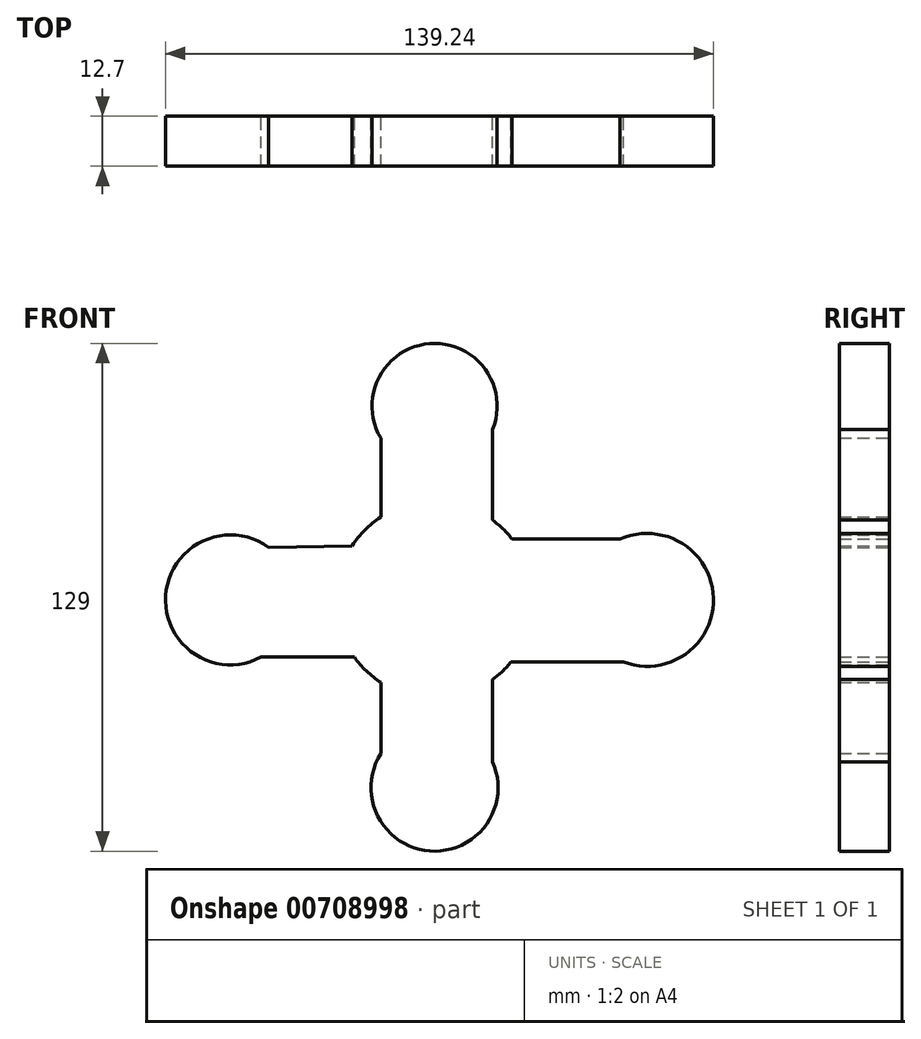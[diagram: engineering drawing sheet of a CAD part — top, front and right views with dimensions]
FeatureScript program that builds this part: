
annotation { "Feature Type Name" : "Feature", "Feature Type Description" : "" }
export const myFeature = defineFeature(function(context is Context, id is Id, definition is map)
    precondition{}
    {
        {
            var Q0;
            Q0=qCreatedBy(makeId("Front.planeOp"),FACE);
            var sketch = newSketch(context, id + "F0", { "sketchPlane" : qUnion([Q0])});
            skCircle(sketch, "E0", {"center": v(0, 0) * mm, "radius": 25.04 * mm});
            skCircle(sketch, "E1", {"center": v(0, 49.24) * mm, "radius": 15.9 * mm});
            skCircle(sketch, "E2", {"center": v(-51.87, 0) * mm, "radius": 16.5 * mm});
            skCircle(sketch, "E3", {"center": v(54, 0) * mm, "radius": 16.88 * mm});
            skCircle(sketch, "E4", {"center": v(0, -47.7) * mm, "radius": 16.15 * mm});
            skLineSegment(sketch, "E5", {"start": v(-13.64, 41.07) * mm, "end": v(-13.64, 21) * mm});
            skLineSegment(sketch, "E6", {"start": v(14.74, 43.26) * mm, "end": v(14.74, 20.24) * mm});
            skLineSegment(sketch, "E7", {"start": v(47.15, 15.42) * mm, "end": v(19.72, 15.42) * mm});
            skLineSegment(sketch, "E8", {"start": v(47.97, -15.76) * mm, "end": v(19.46, -15.76) * mm});
            skLineSegment(sketch, "E9", {"start": v(-13.64, -21) * mm, "end": v(-13.64, -39.07) * mm});
            skLineSegment(sketch, "E10", {"start": v(14.74, -20.24) * mm, "end": v(14.74, -44.36) * mm});
            skLineSegment(sketch, "E11", {"start": v(-42.2, 13.37) * mm, "end": v(-20.92, 13.75) * mm});
            skLineSegment(sketch, "E12", {"start": v(-44.1, -14.55) * mm, "end": v(-20.38, -14.55) * mm});
            skSolve(sketch);
        }
        {
            var Q0;
            {var subQ0=sQuery(id+"F0.wireOp",EDGE,"E4");var subQ1=makeQuery(id+"F0.imprint","INTERSECT",VERTEX,{"derivedFrom":[subQ0,sQuery(id+"F0.wireOp",EDGE,"E9")]});Q0=makeQuery(id+"F0.imprint","IMPRINT",FACE,{"disambiguationData":[TD([[makeQuery(id+"F0.imprint","IMPRINT",EDGE,{"disambiguationData":[TD([[subQ1,1.0]])],"derivedFrom":subQ0}),1.0]])]});}
            var Q1;
            {var subQ0=sQuery(id+"F0.wireOp",EDGE,"E1");var subQ1=makeQuery(id+"F0.imprint","INTERSECT",VERTEX,{"derivedFrom":[subQ0,sQuery(id+"F0.wireOp",EDGE,"E5")]});Q1=makeQuery(id+"F0.imprint","IMPRINT",FACE,{"disambiguationData":[TD([[makeQuery(id+"F0.imprint","IMPRINT",EDGE,{"disambiguationData":[TD([[subQ1,-1.0]])],"derivedFrom":subQ0}),1.0]])]});}
            var Q2;
            {var subQ0=sQuery(id+"F0.wireOp",EDGE,"E11");Q2=makeQuery(id+"F0.imprint","IMPRINT",FACE,{"disambiguationData":[TD([[makeQuery(id+"F0.imprint","IMPRINT",EDGE,{"derivedFrom":subQ0}),-1.0]])]});}
            var Q3;
            {var subQ0=sQuery(id+"F0.wireOp",EDGE,"E9");Q3=makeQuery(id+"F0.imprint","IMPRINT",FACE,{"disambiguationData":[TD([[makeQuery(id+"F0.imprint","IMPRINT",EDGE,{"derivedFrom":subQ0}),1.0]])]});}
            var Q4;
            {var subQ0=sQuery(id+"F0.wireOp",EDGE,"E3");var subQ1=makeQuery(id+"F0.imprint","INTERSECT",VERTEX,{"derivedFrom":[subQ0,sQuery(id+"F0.wireOp",EDGE,"E7")]});Q4=makeQuery(id+"F0.imprint","IMPRINT",FACE,{"disambiguationData":[TD([[makeQuery(id+"F0.imprint","IMPRINT",EDGE,{"disambiguationData":[TD([[subQ1,-1.0]])],"derivedFrom":subQ0}),1.0]])]});}
            var Q5;
            {var subQ0=sQuery(id+"F0.wireOp",EDGE,"E5");Q5=makeQuery(id+"F0.imprint","IMPRINT",FACE,{"disambiguationData":[TD([[makeQuery(id+"F0.imprint","IMPRINT",EDGE,{"derivedFrom":subQ0}),1.0]])]});}
            var Q6;
            {var subQ0=sQuery(id+"F0.wireOp",EDGE,"E2");var subQ1=makeQuery(id+"F0.imprint","INTERSECT",VERTEX,{"derivedFrom":[subQ0,sQuery(id+"F0.wireOp",EDGE,"E11")]});Q6=makeQuery(id+"F0.imprint","IMPRINT",FACE,{"disambiguationData":[TD([[makeQuery(id+"F0.imprint","IMPRINT",EDGE,{"disambiguationData":[TD([[subQ1,-1.0]])],"derivedFrom":subQ0}),1.0]])]});}
            var Q7;
            {var subQ0=sQuery(id+"F0.wireOp",EDGE,"E0");var subQ4=makeQuery(id+"F0.imprint","INTERSECT",VERTEX,{"derivedFrom":[subQ0,sQuery(id+"F0.wireOp",EDGE,"E6")]});Q7=makeQuery(id+"F0.imprint","IMPRINT",FACE,{"disambiguationData":[TD([[makeQuery(id+"F0.imprint","IMPRINT",EDGE,{"disambiguationData":[TD([[subQ4,1.0]])],"derivedFrom":subQ0}),1.0]])]});}
            var Q8;
            {var subQ0=sQuery(id+"F0.wireOp",EDGE,"E7");Q8=makeQuery(id+"F0.imprint","IMPRINT",FACE,{"disambiguationData":[TD([[makeQuery(id+"F0.imprint","IMPRINT",EDGE,{"derivedFrom":subQ0}),1.0]])]});}
            extrude(context, id + "F1", {"entities" : qUnion([Q0, Q1, Q2, Q3, Q4, Q5, Q6, Q7, Q8]), "depth" : 12.7 * mm, "offsetDistance" : 25.4 * mm});
        }
    });
